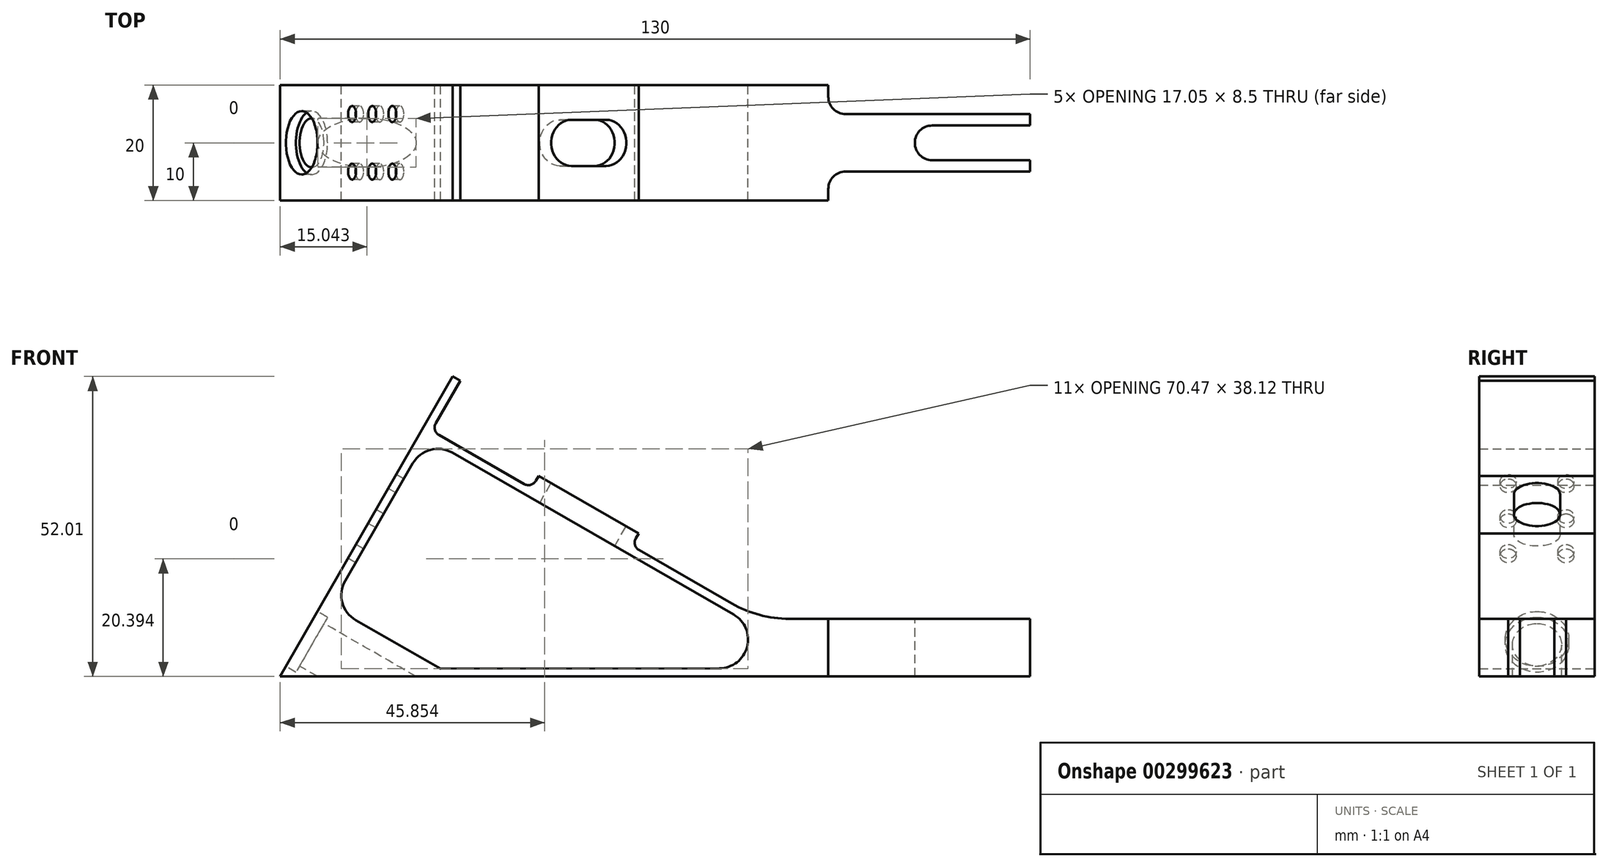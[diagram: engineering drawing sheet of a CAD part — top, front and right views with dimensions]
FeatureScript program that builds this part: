
annotation { "Feature Type Name" : "Feature", "Feature Type Description" : "" }
export const myFeature = defineFeature(function(context is Context, id is Id, definition is map)
    precondition{}
    {
        {
            var Q0;
            Q0=qCreatedBy(makeId("Front.planeOp"),FACE);
            var sketch = newSketch(context, id + "F0", { "sketchPlane" : qUnion([Q0])});
            skLineSegment(sketch, "E0", {"start": v(0, 0) * mm, "end": v(29.91, 52.01) * mm});
            skLineSegment(sketch, "E1", {"start": v(29.91, 52.01) * mm, "end": v(31.21, 51.26) * mm});
            skLineSegment(sketch, "E2", {"start": v(31.21, 51.26) * mm, "end": v(26.98, 43.9) * mm});
            skLineSegment(sketch, "E3", {"start": v(27.53, 41.85) * mm, "end": v(42.27, 33.37) * mm});
            skLineSegment(sketch, "E4", {"start": v(44.31, 33.92) * mm, "end": v(44.81, 34.8) * mm});
            skLineSegment(sketch, "E5", {"start": v(44.81, 34.8) * mm, "end": v(62.15, 24.82) * mm});
            skLineSegment(sketch, "E6", {"start": v(61.65, 23.95) * mm, "end": v(62.15, 24.82) * mm});
            skLineSegment(sketch, "E7", {"start": v(62.2, 21.9) * mm, "end": v(78.27, 12.66) * mm});
            skLineSegment(sketch, "E8", {"start": v(88.24, 10) * mm, "end": v(130, 10) * mm});
            skLineSegment(sketch, "E9", {"start": v(130, 10) * mm, "end": v(130, 0) * mm});
            skLineSegment(sketch, "E10", {"start": v(130, 0) * mm, "end": v(0, 0) * mm});
            skLineSegment(sketch, "E11", {"start": v(130, 0) * mm, "end": v(-60.3, -0.31) * mm, "construction": true});
            skPoint(sketch, "E12.visualSharp", {"position": v(82.9, 10) * mm});
            skArc(sketch, "E12.filletArc", {"start": v(78.27, 12.66) * mm, "mid": v(83.08, 10.68) * mm, "end": v(88.24, 10) * mm});
            skPoint(sketch, "E13.visualSharp", {"position": v(60.9, 22.65) * mm});
            skArc(sketch, "E13.filletArc", {"start": v(61.65, 23.95) * mm, "mid": v(61.5, 22.81) * mm, "end": v(62.2, 21.9) * mm});
            skPoint(sketch, "E14.visualSharp", {"position": v(43.57, 32.62) * mm});
            skArc(sketch, "E14.filletArc", {"start": v(42.27, 33.37) * mm, "mid": v(43.4, 33.22) * mm, "end": v(44.31, 33.92) * mm});
            skPoint(sketch, "E15.visualSharp", {"position": v(26.23, 42.6) * mm});
            skArc(sketch, "E15.filletArc", {"start": v(26.98, 43.9) * mm, "mid": v(26.83, 42.76) * mm, "end": v(27.53, 41.85) * mm});
            skLineSegment(sketch, "E16", {"start": v(13.11, 9.76) * mm, "end": v(27.77, 1.33) * mm});
            skLineSegment(sketch, "E17", {"start": v(27.77, 1.33) * mm, "end": v(76.11, 1.41) * mm});
            skLineSegment(sketch, "E18", {"start": v(11.27, 16.59) * mm, "end": v(22.99, 36.96) * mm});
            skLineSegment(sketch, "E19", {"start": v(78.6, 10.75) * mm, "end": v(29.82, 38.8) * mm});
            skPoint(sketch, "E20.visualSharp", {"position": v(94.77, 1.44) * mm});
            skArc(sketch, "E20.filletArc", {"start": v(76.11, 1.41) * mm, "mid": v(80.93, 5.13) * mm, "end": v(78.6, 10.75) * mm});
            skPoint(sketch, "E21.visualSharp", {"position": v(25.48, 41.3) * mm});
            skArc(sketch, "E21.filletArc", {"start": v(29.82, 38.8) * mm, "mid": v(26.02, 39.3) * mm, "end": v(22.99, 36.96) * mm});
            skArc(sketch, "E22.filletArc", {"start": v(11.27, 16.59) * mm, "mid": v(10.78, 12.8) * mm, "end": v(13.11, 9.76) * mm});
            skSolve(sketch);
        }
        {
            var Q0;
            Q0=makeQuery(id+"F0.imprint","IMPRINT",FACE,{"disambiguationData":[TD([[makeQuery(id+"F0.imprint","IMPRINT",EDGE,{"derivedFrom":sQuery(id+"F0.wireOp",EDGE,"E0")}),-1.0]])]});
            extrude(context, id + "F1", {"entities" : qUnion([Q0]), "depth" : 20 * mm});
        }
        {
            var Q0;
            Q0=makeQuery(id+"F1.opExtrude","SWEPT_FACE",FACE,{"disambiguationData":[OSD([sQuery(id+"F0.wireOp",EDGE,"E0")])]});
            var sketch = newSketch(context, id + "F2", { "sketchPlane" : qUnion([Q0])});
            skCircle(sketch, "E23", {"center": v(10, 7.5) * mm, "radius": 5.5 * mm});
            skCircle(sketch, "E24", {"center": v(10, 7.5) * mm, "radius": 4.25 * mm});
            skCircle(sketch, "E25", {"center": v(5, 39) * mm, "radius": 1.4 * mm});
            skCircle(sketch, "E26", {"center": v(15, 39) * mm, "radius": 1.4 * mm});
            skCircle(sketch, "E27", {"center": v(5, 32) * mm, "radius": 1.4 * mm});
            skCircle(sketch, "E28", {"center": v(15, 32) * mm, "radius": 1.4 * mm});
            skCircle(sketch, "E29", {"center": v(5, 25) * mm, "radius": 1.4 * mm});
            skCircle(sketch, "E30", {"center": v(15, 25) * mm, "radius": 1.4 * mm});
            skSolve(sketch);
        }
        {
            var Q0;
            Q0=makeQuery(id+"F2.imprint","IMPRINT",FACE,{"disambiguationData":[TD([[makeQuery(id+"F2.imprint","IMPRINT",EDGE,{"derivedFrom":sQuery(id+"F2.wireOp",EDGE,"E24")}),1.0]])]});
            var Q1;
            Q1=makeQuery(id+"F2.imprint","IMPRINT",FACE,{"disambiguationData":[TD([[makeQuery(id+"F2.imprint","IMPRINT",EDGE,{"derivedFrom":sQuery(id+"F2.wireOp",EDGE,"E25")}),1.0]])]});
            var Q2;
            Q2=makeQuery(id+"F2.imprint","IMPRINT",FACE,{"disambiguationData":[TD([[makeQuery(id+"F2.imprint","IMPRINT",EDGE,{"derivedFrom":sQuery(id+"F2.wireOp",EDGE,"E27")}),1.0]])]});
            var Q3;
            Q3=makeQuery(id+"F2.imprint","IMPRINT",FACE,{"disambiguationData":[TD([[makeQuery(id+"F2.imprint","IMPRINT",EDGE,{"derivedFrom":sQuery(id+"F2.wireOp",EDGE,"E28")}),1.0]])]});
            var Q4;
            Q4=makeQuery(id+"F2.imprint","IMPRINT",FACE,{"disambiguationData":[TD([[makeQuery(id+"F2.imprint","IMPRINT",EDGE,{"derivedFrom":sQuery(id+"F2.wireOp",EDGE,"E26")}),1.0]])]});
            var Q5;
            Q5=makeQuery(id+"F2.imprint","IMPRINT",FACE,{"disambiguationData":[TD([[makeQuery(id+"F2.imprint","IMPRINT",EDGE,{"derivedFrom":sQuery(id+"F2.wireOp",EDGE,"E29")}),1.0]])]});
            var Q6;
            Q6=makeQuery(id+"F2.imprint","IMPRINT",FACE,{"disambiguationData":[TD([[makeQuery(id+"F2.imprint","IMPRINT",EDGE,{"derivedFrom":sQuery(id+"F2.wireOp",EDGE,"E30")}),1.0]])]});
            extrude(context, id + "F3", {"entities" : qUnion([Q0, Q1, Q2, Q3, Q4, Q5, Q6]), "operationType" : NewBodyOperationType.REMOVE, "oppositeDirection" : true, "depth" : 30 * mm});
        }
        {
            var Q0;
            Q0=makeQuery(id+"F2.imprint","IMPRINT",FACE,{"disambiguationData":[TD([[makeQuery(id+"F2.imprint","IMPRINT",EDGE,{"derivedFrom":sQuery(id+"F2.wireOp",EDGE,"E23")}),1.0]])]});
            var Q1;
            Q1=sQuery(id+"F2.wireOp",EDGE,"E23");
            extrude(context, id + "F4", {"entities" : qUnion([Q0]), "operationType" : NewBodyOperationType.REMOVE, "surfaceEntities" : qUnion([Q1]), "oppositeDirection" : true, "depth" : 2 * mm});
        }
        {
            var Q0;
            Q0=makeQuery(id+"F1.opExtrude","SWEPT_FACE",FACE,{"disambiguationData":[OSD([sQuery(id+"F0.wireOp",EDGE,"E8")])]});
            var sketch = newSketch(context, id + "F5", { "sketchPlane" : qUnion([Q0])});
            skLineSegment(sketch, "E31", {"start": v(95, -20) * mm, "end": v(95, -18) * mm});
            skLineSegment(sketch, "E32", {"start": v(98, -15) * mm, "end": v(130, -15) * mm});
            skLineSegment(sketch, "E33", {"start": v(130, -5) * mm, "end": v(98, -5) * mm});
            skLineSegment(sketch, "E34", {"start": v(95, -2) * mm, "end": v(95, 0) * mm});
            skPoint(sketch, "E35.visualSharp", {"position": v(171.5, -5.83) * mm});
            skPoint(sketch, "E36.visualSharp", {"position": v(92.25, -10.09) * mm});
            skPoint(sketch, "E37.visualSharp", {"position": v(95, -5) * mm});
            skArc(sketch, "E37.filletArc", {"start": v(95, -2) * mm, "mid": v(95.88, -4.12) * mm, "end": v(98, -5) * mm});
            skPoint(sketch, "E38.visualSharp", {"position": v(95, -15) * mm});
            skArc(sketch, "E38.filletArc", {"start": v(98, -15) * mm, "mid": v(95.88, -15.88) * mm, "end": v(95, -18) * mm});
            skSolve(sketch);
        }
        {
            var Q0;
            Q0 = qSketchRegion(id + "F5", true);
            var Q1;
            {var subQ5=sQuery(id+"F5.wireOp",EDGE,"E31");Q1=makeQuery(id+"F5.imprint","IMPRINT",FACE,{"disambiguationData":[TD([[makeQuery(id+"F5.imprint","IMPRINT",EDGE,{"derivedFrom":subQ5}),-1.0]])]});}
            var Q2;
            {var subQ5=sQuery(id+"F5.wireOp",EDGE,"E33");Q2=makeQuery(id+"F5.imprint","IMPRINT",FACE,{"disambiguationData":[TD([[makeQuery(id+"F5.imprint","IMPRINT",EDGE,{"derivedFrom":subQ5}),-1.0]])]});}
            extrude(context, id + "F6", {"entities" : qUnion([Q0, Q1, Q2]), "operationType" : NewBodyOperationType.REMOVE, "oppositeDirection" : true, "depth" : 25 * mm});
        }
        {
            var Q0;
            Q0=makeQuery(id+"F1.opExtrude","SWEPT_FACE",FACE,{"disambiguationData":[OSD([sQuery(id+"F0.wireOp",EDGE,"E8")])]});
            var sketch = newSketch(context, id + "F7", { "sketchPlane" : qUnion([Q0])});
            skLineSegment(sketch, "E39", {"start": v(130, -7) * mm, "end": v(113, -7) * mm});
            skArc(sketch, "E40", {"start": v(113, -7) * mm, "mid": v(110, -10) * mm, "end": v(113, -13) * mm});
            skLineSegment(sketch, "E41", {"start": v(113, -13) * mm, "end": v(130, -13) * mm});
            skSolve(sketch);
        }
        {
            var Q0;
            Q0 = qSketchRegion(id + "F7", true);
            var Q1;
            {var subQ0=sQuery(id+"F7.wireOp",EDGE,"E39");Q1=makeQuery(id+"F7.imprint","IMPRINT",FACE,{"disambiguationData":[TD([[makeQuery(id+"F7.imprint","IMPRINT",EDGE,{"derivedFrom":subQ0}),1.0]])]});}
            extrude(context, id + "F8", {"entities" : qUnion([Q0, Q1]), "operationType" : NewBodyOperationType.REMOVE, "endBound" : BoundingType.THROUGH_ALL, "oppositeDirection" : true, "depth" : 25 * mm});
        }
        {
            var Q0;
            Q0=makeQuery(id+"F1.opExtrude","SWEPT_FACE",FACE,{"disambiguationData":[OSD([sQuery(id+"F0.wireOp",EDGE,"E5")])]});
            var sketch = newSketch(context, id + "F9", { "sketchPlane" : qUnion([Q0])});
            skLineSegment(sketch, "E42", {"start": v(28, -10) * mm, "end": v(35, -10) * mm, "construction": true});
            skArc(sketch, "E43.0.startCap", {"start": v(28, -14) * mm, "mid": v(24, -10) * mm, "end": v(28, -6) * mm});
            skArc(sketch, "E43.0.endCap", {"start": v(35, -6) * mm, "mid": v(39, -10) * mm, "end": v(35, -14) * mm});
            skLineSegment(sketch, "E43.0.left", {"start": v(28, -6) * mm, "end": v(35, -6) * mm});
            skLineSegment(sketch, "E43.0.right", {"start": v(28, -14) * mm, "end": v(35, -14) * mm});
            skSolve(sketch);
        }
        {
            var Q0;
            Q0 = qSketchRegion(id + "F9", true);
            extrude(context, id + "F10", {"entities" : qUnion([Q0]), "operationType" : NewBodyOperationType.REMOVE, "oppositeDirection" : true, "depth" : 15 * mm});
        }
    });
